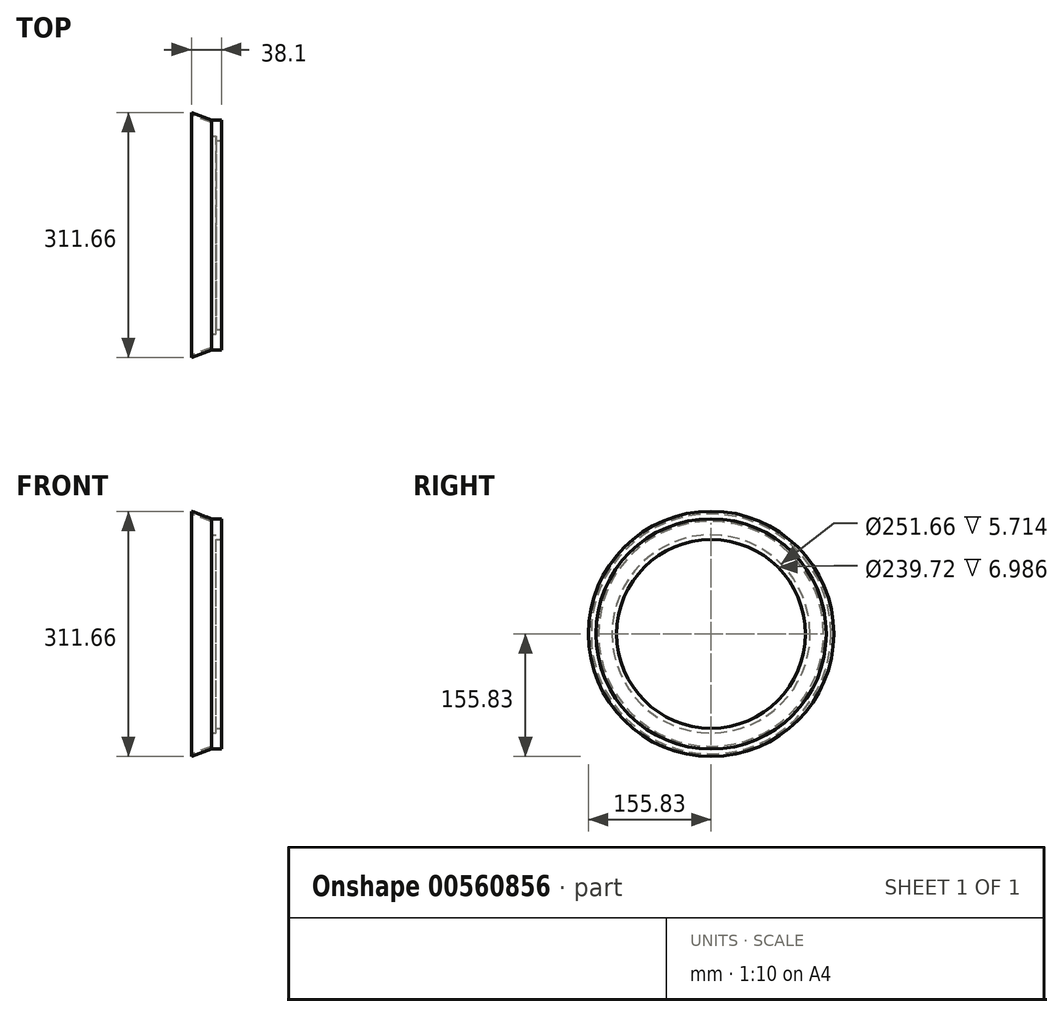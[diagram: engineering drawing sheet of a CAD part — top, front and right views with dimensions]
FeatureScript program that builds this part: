
annotation { "Feature Type Name" : "Feature", "Feature Type Description" : "" }
export const myFeature = defineFeature(function(context is Context, id is Id, definition is map)
    precondition{}
    {
        {
            var Q0;
            Q0=qCreatedBy(makeId("Front.planeOp"),FACE);
            var sketch = newSketch(context, id + "F0", { "sketchPlane" : qUnion([Q0])});
            skLineSegment(sketch, "E0", {"start": v(0, 0) * mm, "end": v(29.52, 0) * mm, "construction": true});
            skLineSegment(sketch, "E1", {"start": v(0, 152.4) * mm, "end": v(0, 155.83) * mm});
            skLineSegment(sketch, "E2", {"start": v(25.4, 146.3) * mm, "end": v(0, 155.83) * mm});
            skLineSegment(sketch, "E3", {"start": v(25.4, 146.3) * mm, "end": v(25.4, 142.88) * mm});
            skLineSegment(sketch, "E4", {"start": v(25.4, 142.88) * mm, "end": v(0, 152.4) * mm});
            skSolve(sketch);
        }
        {
            var Q0;
            Q0 = qSketchRegion(id + "F0", true);
            var Q1;
            Q1=sQuery(id+"F0.wireOp",EDGE,"E0");
            revolve(context, id + "F1", {"entities" : qUnion([Q0]), "axis" : qUnion([Q1]), "revolveType" : RevolveType.FULL});
        }
        {
            var Q0;
            Q0=makeQuery(id+"F1.opRevolve","SWEPT_FACE",FACE,{"disambiguationData":[OSD([sQuery(id+"F0.wireOp",EDGE,"E3")])]});
            var sketch = newSketch(context, id + "F2", { "sketchPlane" : qUnion([Q0])});
            skCircle(sketch, "E5", {"center": v(0, 0) * mm, "radius": 146.3 * mm});
            skSolve(sketch);
        }
        {
            var Q0;
            Q0 = qSketchRegion(id + "F2", true);
            extrude(context, id + "F3", {"entities" : qUnion([Q0]), "operationType" : NewBodyOperationType.ADD, "depth" : 12.7 * mm, "offsetDistance" : 25.4 * mm});
        }
        {
            var Q0;
            Q0=qCreatedBy(makeId("Front.planeOp"),FACE);
            var sketch = newSketch(context, id + "F4", { "sketchPlane" : qUnion([Q0])});
            skLineSegment(sketch, "E6", {"start": v(25.4, 125.83) * mm, "end": v(31.11, 125.83) * mm});
            skLineSegment(sketch, "E7", {"start": v(31.11, 125.83) * mm, "end": v(31.11, 119.86) * mm});
            skLineSegment(sketch, "E8", {"start": v(31.11, 119.86) * mm, "end": v(38.1, 119.86) * mm});
            skLineSegment(sketch, "E9", {"start": v(38.1, 119.86) * mm, "end": v(38.1, 0) * mm});
            skLineSegment(sketch, "E10", {"start": v(38.1, 0) * mm, "end": v(25.4, 0) * mm});
            skLineSegment(sketch, "E11", {"start": v(25.4, 0) * mm, "end": v(25.4, 125.83) * mm});
            skLineSegment(sketch, "E12", {"start": v(25.4, 0) * mm, "end": v(53.24, 0) * mm, "construction": true});
            skSolve(sketch);
        }
        {
            var Q0;
            Q0 = qSketchRegion(id + "F4", true);
            var Q1;
            Q1=sQuery(id+"F4.wireOp",EDGE,"E12");
            revolve(context, id + "F5", {"operationType" : NewBodyOperationType.REMOVE, "entities" : qUnion([Q0]), "axis" : qUnion([Q1]), "revolveType" : RevolveType.FULL, "oppositeDirection" : true});
        }
    });
